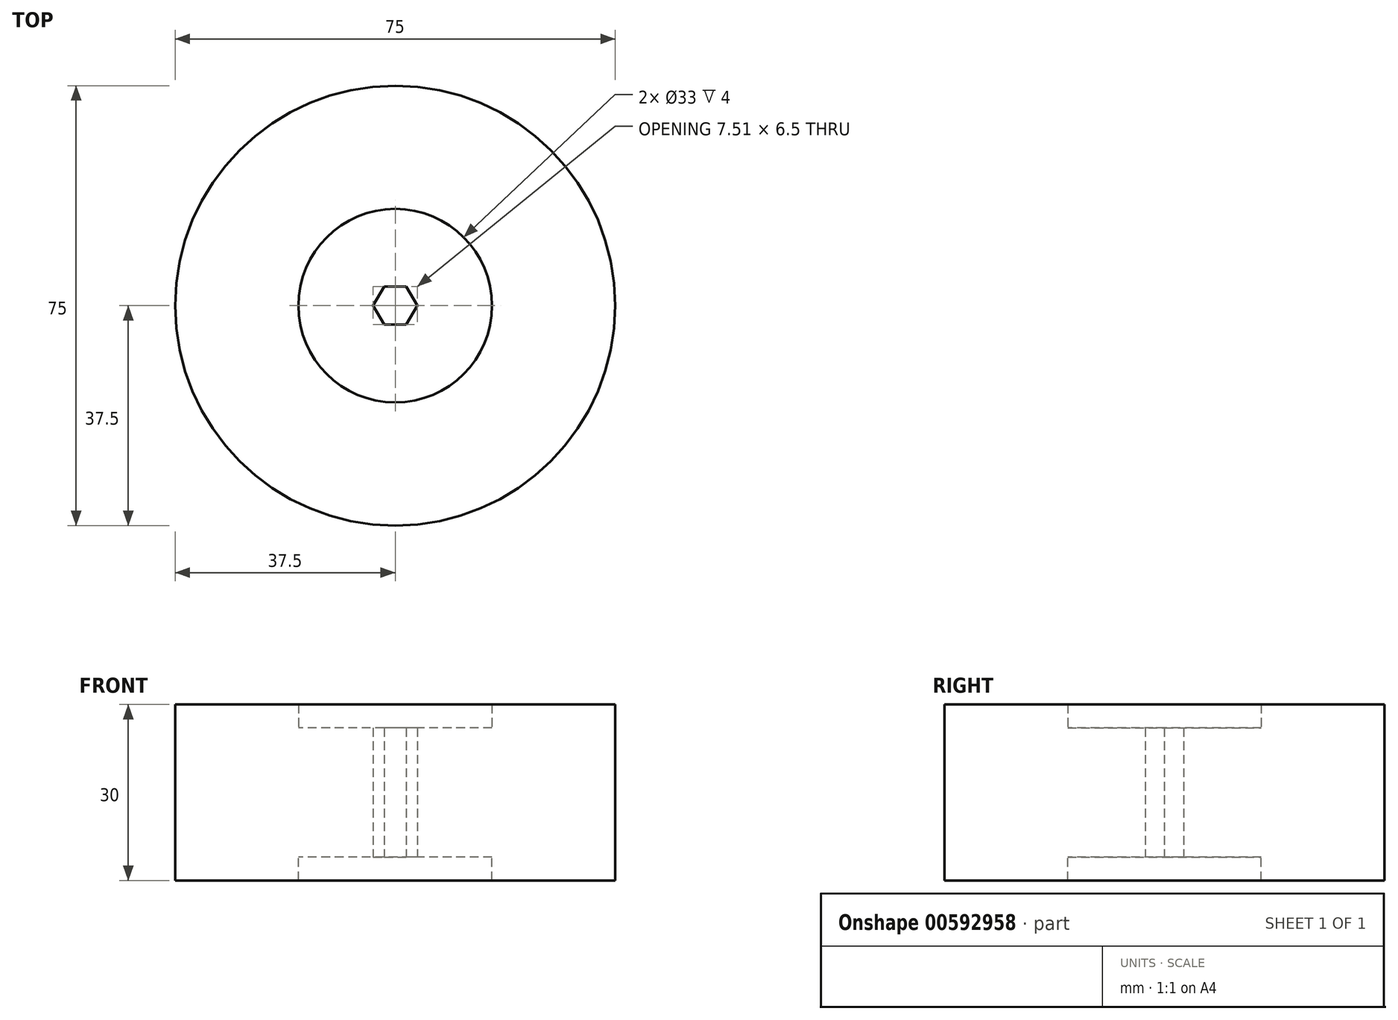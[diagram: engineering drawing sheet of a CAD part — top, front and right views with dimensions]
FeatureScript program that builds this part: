
annotation { "Feature Type Name" : "Feature", "Feature Type Description" : "" }
export const myFeature = defineFeature(function(context is Context, id is Id, definition is map)
    precondition{}
    {
        {
            var Q0;
            Q0=qCreatedBy(makeId("Top.planeOp"),FACE);
            var sketch = newSketch(context, id + "F0", { "sketchPlane" : qUnion([Q0])});
            skCircle(sketch, "E0", {"center": v(0, 0) * mm, "radius": 37.5 * mm});
            skCircle(sketch, "E1", {"center": v(0, 0) * mm, "radius": 16.5 * mm});
            skCircle(sketch, "E2", {"center": v(0, 0) * mm, "radius": 1 * mm});
            skCircle(sketch, "E3.cCircle", {"center": v(0, 0) * mm, "radius": 3.25 * mm, "construction": true});
            skLineSegment(sketch, "E3.0", {"start": v(1.88, -3.25) * mm, "end": v(-1.88, -3.25) * mm});
            skLineSegment(sketch, "E3.1", {"start": v(-1.88, -3.25) * mm, "end": v(-3.75, 0) * mm});
            skLineSegment(sketch, "E3.2", {"start": v(-3.75, 0) * mm, "end": v(-1.88, 3.25) * mm});
            skLineSegment(sketch, "E3.3", {"start": v(-1.88, 3.25) * mm, "end": v(1.88, 3.25) * mm});
            skLineSegment(sketch, "E3.4", {"start": v(1.88, 3.25) * mm, "end": v(3.75, 0) * mm});
            skLineSegment(sketch, "E3.5", {"start": v(3.75, 0) * mm, "end": v(1.88, -3.25) * mm});
            skPoint(sketch, "E3.0.midPoint", {"position": v(0, -3.25) * mm});
            skSolve(sketch);
        }
        {
            var Q0;
            Q0=makeQuery(id+"F0.imprint","IMPRINT",FACE,{"disambiguationData":[TD([[makeQuery(id+"F0.imprint","IMPRINT",EDGE,{"derivedFrom":sQuery(id+"F0.wireOp",EDGE,"xmvv88hr-1nj2-zJQl-Mrmj-24I1aqPNY2UM")}),-1.0]])]});
            var Q1;
            Q1=makeQuery(id+"F0.imprint","IMPRINT",FACE,{"disambiguationData":[TD([[makeQuery(id+"F0.imprint","IMPRINT",EDGE,{"derivedFrom":sQuery(id+"F0.wireOp",EDGE,"E1")}),1.0]])]});
            extrude(context, id + "F1", {"entities" : qUnion([Q0, Q1]), "depth" : 22 * mm, "offsetDistance" : 25 * mm});
        }
        {
            var Q0;
            Q0=makeQuery(id+"F0.imprint","IMPRINT",FACE,{"disambiguationData":[TD([[makeQuery(id+"F0.imprint","IMPRINT",EDGE,{"derivedFrom":sQuery(id+"F0.wireOp",EDGE,"E0")}),1.0]])]});
            extrude(context, id + "F2", {"entities" : qUnion([Q0]), "operationType" : NewBodyOperationType.ADD, "depth" : 26 * mm, "offsetDistance" : 25 * mm});
        }
        {
            var Q0;
            Q0=makeQuery(id+"F0.imprint","IMPRINT",FACE,{"disambiguationData":[TD([[makeQuery(id+"F0.imprint","IMPRINT",EDGE,{"derivedFrom":sQuery(id+"F0.wireOp",EDGE,"E0")}),1.0]])]});
            extrude(context, id + "F3", {"entities" : qUnion([Q0]), "operationType" : NewBodyOperationType.ADD, "depth" : -4 * mm, "offsetDistance" : 25 * mm});
        }
    });
